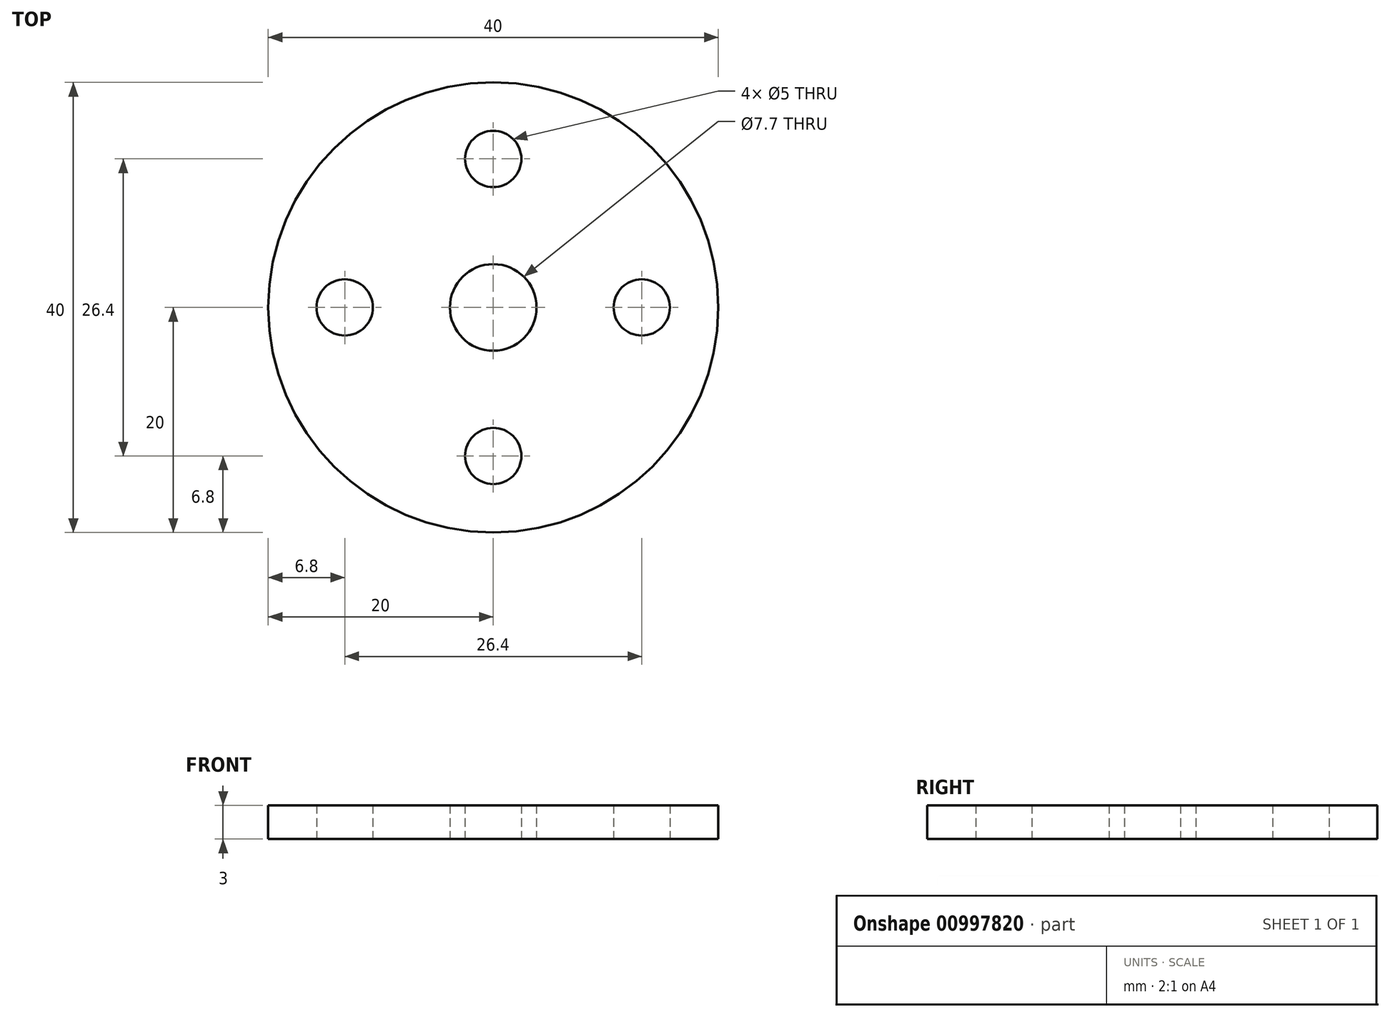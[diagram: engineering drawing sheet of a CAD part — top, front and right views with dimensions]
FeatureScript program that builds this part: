
annotation { "Feature Type Name" : "Feature", "Feature Type Description" : "" }
export const myFeature = defineFeature(function(context is Context, id is Id, definition is map)
    precondition{}
    {
        {
            var Q0;
            Q0=qCreatedBy(makeId("Top.planeOp"),FACE);
            var sketch = newSketch(context, id + "F0", { "sketchPlane" : qUnion([Q0])});
            skCircle(sketch, "E0", {"center": v(0, 0) * mm, "radius": 20 * mm});
            skCircle(sketch, "E1", {"center": v(0, 0) * mm, "radius": 3.85 * mm});
            skLineSegment(sketch, "E2", {"start": v(0, 0) * mm, "end": v(0, 13.2) * mm, "construction": true});
            skCircle(sketch, "E3", {"center": v(0, 13.2) * mm, "radius": 2.5 * mm});
            skCircle(sketch, "E4.1.0", {"center": v(-13.2, 0) * mm, "radius": 2.5 * mm});
            skCircle(sketch, "E4.2.0", {"center": v(0, -13.2) * mm, "radius": 2.5 * mm});
            skCircle(sketch, "E4.3.0", {"center": v(13.2, 0) * mm, "radius": 2.5 * mm});
            skSolve(sketch);
        }
        {
            var Q0;
            Q0 = qSketchRegion(id + "F0", true);
            extrude(context, id + "F1", {"entities" : qUnion([Q0]), "depth" : 3 * mm, "offsetDistance" : 25 * mm});
        }
    });
